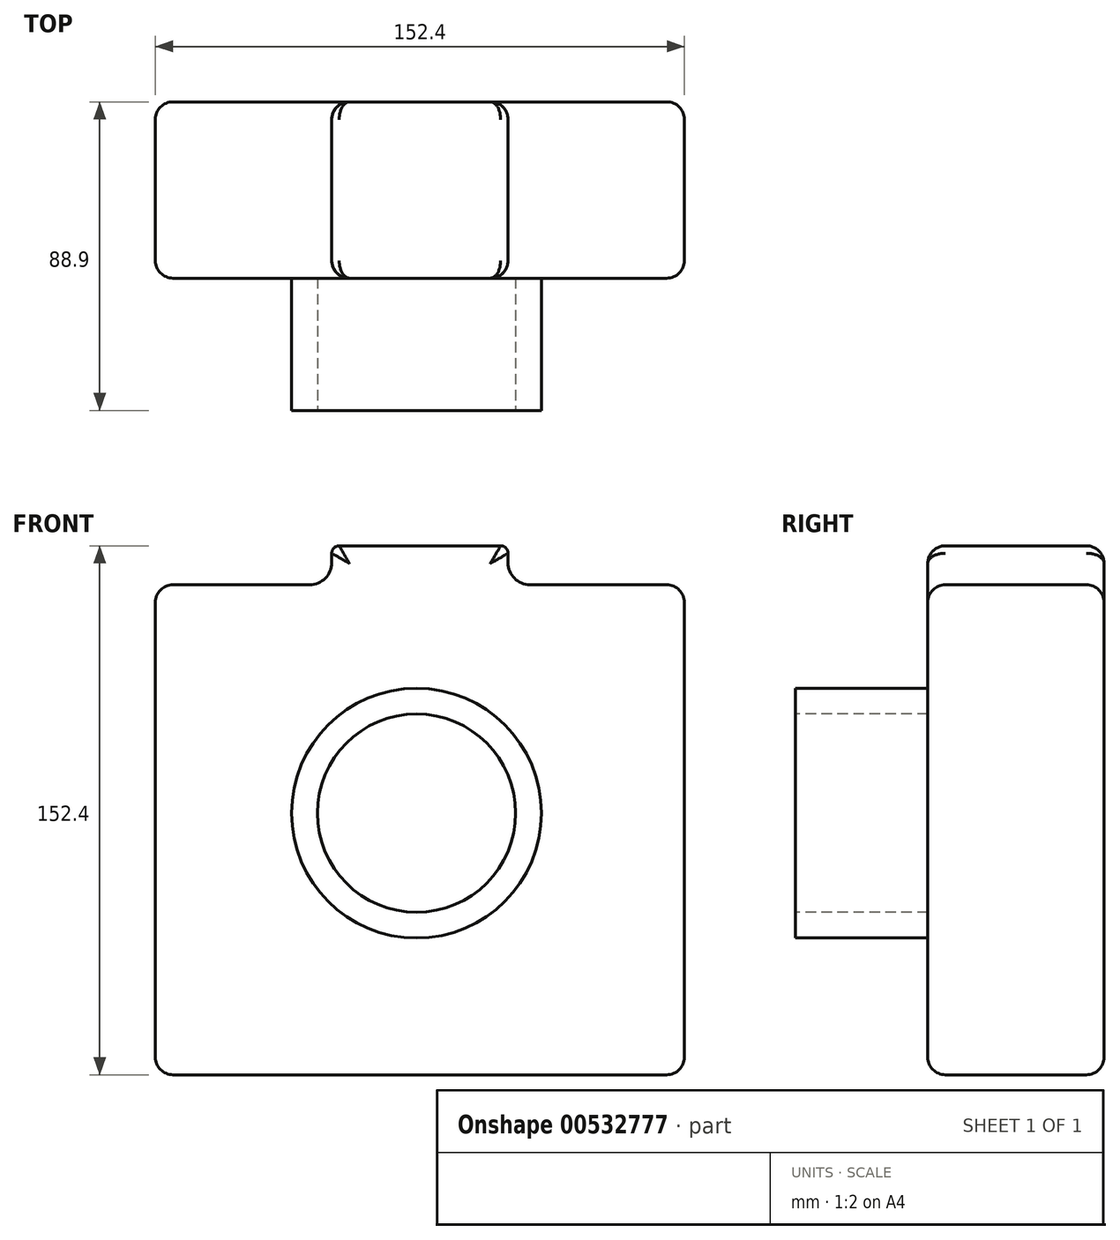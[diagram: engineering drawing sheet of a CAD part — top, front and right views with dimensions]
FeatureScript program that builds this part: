
annotation { "Feature Type Name" : "Feature", "Feature Type Description" : "" }
export const myFeature = defineFeature(function(context is Context, id is Id, definition is map)
    precondition{}
    {
        {
            var Q0;
            Q0=qCreatedBy(makeId("Front.planeOp"),FACE);
            var sketch = newSketch(context, id + "F0", { "sketchPlane" : qUnion([Q0])});
            skLineSegment(sketch, "E0.bottom", {"start": v(-75.22, 77.03) * mm, "end": v(77.18, 77.03) * mm});
            skLineSegment(sketch, "E0.top", {"start": v(-75.22, -75.37) * mm, "end": v(77.18, -75.37) * mm});
            skLineSegment(sketch, "E0.left", {"start": v(-75.22, 77.03) * mm, "end": v(-75.22, -75.37) * mm});
            skLineSegment(sketch, "E0.right", {"start": v(77.18, 77.03) * mm, "end": v(77.18, -75.37) * mm});
            skLineSegment(sketch, "E1.bottom", {"start": v(-22.27, 77.03) * mm, "end": v(24.22, 77.03) * mm});
            skLineSegment(sketch, "E1.top", {"start": v(-24.42, 65.8) * mm, "end": v(26.38, 65.8) * mm});
            skLineSegment(sketch, "E1.left", {"start": v(-24.42, 74.88) * mm, "end": v(-24.42, 72.16) * mm});
            skLineSegment(sketch, "E1.right", {"start": v(26.38, 74.88) * mm, "end": v(26.38, 72.16) * mm});
            skLineSegment(sketch, "E2", {"start": v(-24.42, 65.8) * mm, "end": v(-75.22, 65.8) * mm});
            skLineSegment(sketch, "E3", {"start": v(-75.22, 65.8) * mm, "end": v(-30.77, 65.8) * mm});
            skLineSegment(sketch, "E4", {"start": v(77.18, 65.8) * mm, "end": v(32.73, 65.8) * mm});
            skArc(sketch, "E5.filletArc", {"start": v(-30.77, 65.8) * mm, "mid": v(-26.28, 67.67) * mm, "end": v(-24.42, 72.16) * mm});
            skPoint(sketch, "E6.visualSharp", {"position": v(26.38, 65.8) * mm});
            skArc(sketch, "E6.filletArc", {"start": v(26.38, 72.16) * mm, "mid": v(28.24, 67.67) * mm, "end": v(32.73, 65.8) * mm});
            skPoint(sketch, "E7.visualSharp", {"position": v(-24.42, 77.03) * mm});
            skArc(sketch, "E7.filletArc", {"start": v(-22.27, 77.03) * mm, "mid": v(-23.8, 76.4) * mm, "end": v(-24.42, 74.88) * mm});
            skPoint(sketch, "E8.visualSharp", {"position": v(26.38, 77.03) * mm});
            skArc(sketch, "E8.filletArc", {"start": v(26.38, 74.88) * mm, "mid": v(25.75, 76.4) * mm, "end": v(24.22, 77.03) * mm});
            skSolve(sketch);
        }
        {
            var Q0;
            {var subQ2=sQuery(id+"F0.wireOp",EDGE,"E0.top");Q0=makeQuery(id+"F0.imprint","IMPRINT",FACE,{"disambiguationData":[TD([[makeQuery(id+"F0.imprint","IMPRINT",EDGE,{"derivedFrom":subQ2}),1.0]])]});}
            extrude(context, id + "F1", {"entities" : qUnion([Q0]), "depth" : 50.8 * mm, "offsetDistance" : 25.4 * mm});
        }
        {
            var Q0;
            Q0=makeQuery(id+"F1.opExtrude","CAP_FACE",FACE,{"disambiguationData":[OSD([sQuery(id+"F0.wireOp",EDGE,"E0.top"),sQuery(id+"F0.wireOp",EDGE,"E0.left"),sQuery(id+"F0.wireOp",EDGE,"E0.right"),sQuery(id+"F0.wireOp",EDGE,"E1.bottom"),sQuery(id+"F0.wireOp",EDGE,"E1.left"),sQuery(id+"F0.wireOp",EDGE,"E1.right"),sQuery(id+"F0.wireOp",EDGE,"E3"),sQuery(id+"F0.wireOp",EDGE,"E4"),sQuery(id+"F0.wireOp",EDGE,"E5.filletArc"),sQuery(id+"F0.wireOp",EDGE,"E6.filletArc"),sQuery(id+"F0.wireOp",EDGE,"E7.filletArc"),sQuery(id+"F0.wireOp",EDGE,"E8.filletArc")])],"isStart":false});
            var sketch = newSketch(context, id + "F2", { "sketchPlane" : qUnion([Q0])});
            skCircle(sketch, "E9", {"center": v(0, 0) * mm, "radius": 35.98 * mm});
            skSolve(sketch);
        }
        {
            var Q0;
            Q0 = qSketchRegion(id + "F2", true);
            extrude(context, id + "F3", {"entities" : qUnion([Q0]), "operationType" : NewBodyOperationType.ADD, "depth" : 38.1 * mm, "offsetDistance" : 25.4 * mm});
        }
        {
            var Q0;
            Q0=makeQuery(id+"F3.opExtrude","CAP_FACE",FACE,{"disambiguationData":[OSD([sQuery(id+"F2.wireOp",EDGE,"E9")])],"isStart":false});
            var sketch = newSketch(context, id + "F4", { "sketchPlane" : qUnion([Q0])});
            skCircle(sketch, "E10", {"center": v(0, 0) * mm, "radius": 28.56 * mm});
            skSolve(sketch);
        }
        {
            var Q0;
            Q0=makeQuery(id+"F4.imprint","IMPRINT",FACE,{"disambiguationData":[TD([[makeQuery(id+"F4.imprint","IMPRINT",EDGE,{"derivedFrom":sQuery(id+"F4.wireOp",EDGE,"E10")}),1.0]])]});
            extrude(context, id + "F5", {"entities" : qUnion([Q0]), "operationType" : NewBodyOperationType.REMOVE, "oppositeDirection" : true, "depth" : 38.1 * mm, "offsetDistance" : 25.4 * mm});
        }
        {
            var Q0;
            Q0=makeQuery(id+"F1.opExtrude","CAP_EDGE",EDGE,{"disambiguationData":[OSD([sQuery(id+"F0.wireOp",EDGE,"E0.left")])],"isStart":false});
            var Q1;
            Q1=makeQuery(id+"F1.opExtrude","SWEPT_EDGE",EDGE,{"disambiguationData":[OSD([sQuery(id+"F0.wireOp",EDGE,"E0.left"),sQuery(id+"F0.wireOp",EDGE,"E3")])]});
            var Q2;
            Q2=makeQuery(id+"F1.opExtrude","CAP_EDGE",EDGE,{"disambiguationData":[OSD([sQuery(id+"F0.wireOp",EDGE,"E0.left")])],"isStart":true});
            var Q3;
            Q3=makeQuery(id+"F1.opExtrude","SWEPT_EDGE",EDGE,{"disambiguationData":[OSD([sQuery(id+"F0.wireOp",EDGE,"E0.top"),sQuery(id+"F0.wireOp",EDGE,"E0.left")])]});
            var Q4;
            Q4=makeQuery(id+"F1.opExtrude","CAP_EDGE",EDGE,{"disambiguationData":[OSD([sQuery(id+"F0.wireOp",EDGE,"E0.top")])],"isStart":false});
            var Q5;
            Q5=makeQuery(id+"F1.opExtrude","CAP_EDGE",EDGE,{"disambiguationData":[OSD([sQuery(id+"F0.wireOp",EDGE,"E0.right")])],"isStart":false});
            var Q6;
            Q6=makeQuery(id+"F1.opExtrude","SWEPT_EDGE",EDGE,{"disambiguationData":[OSD([sQuery(id+"F0.wireOp",EDGE,"E0.right"),sQuery(id+"F0.wireOp",EDGE,"E4")])]});
            var Q7;
            Q7=makeQuery(id+"F1.opExtrude","CAP_EDGE",EDGE,{"disambiguationData":[OSD([sQuery(id+"F0.wireOp",EDGE,"E4")])],"isStart":false});
            var Q8;
            Q8=makeQuery(id+"F1.opExtrude","SWEPT_EDGE",EDGE,{"disambiguationData":[OSD([sQuery(id+"F0.wireOp",EDGE,"E0.top"),sQuery(id+"F0.wireOp",EDGE,"E0.right")])]});
            var Q9;
            Q9=makeQuery(id+"F1.opExtrude","CAP_EDGE",EDGE,{"disambiguationData":[OSD([sQuery(id+"F0.wireOp",EDGE,"E0.right")])],"isStart":true});
            var Q10;
            Q10=makeQuery(id+"F1.opExtrude","CAP_EDGE",EDGE,{"disambiguationData":[OSD([sQuery(id+"F0.wireOp",EDGE,"E4")])],"isStart":true});
            var Q11;
            Q11=makeQuery(id+"F1.opExtrude","CAP_EDGE",EDGE,{"disambiguationData":[OSD([sQuery(id+"F0.wireOp",EDGE,"E1.bottom")])],"isStart":true});
            var Q12;
            Q12=makeQuery(id+"F1.opExtrude","CAP_EDGE",EDGE,{"disambiguationData":[OSD([sQuery(id+"F0.wireOp",EDGE,"E0.top")])],"isStart":true});
            fillet(context, id + "F6", {"entities" : qUnion([Q0, Q1, Q2, Q3, Q4, Q5, Q6, Q7, Q8, Q9, Q10, Q11, Q12]), "radius" : 5.08 * mm, "tangentPropagation" : true, "allowEdgeOverflow" : false});
        }
    });
